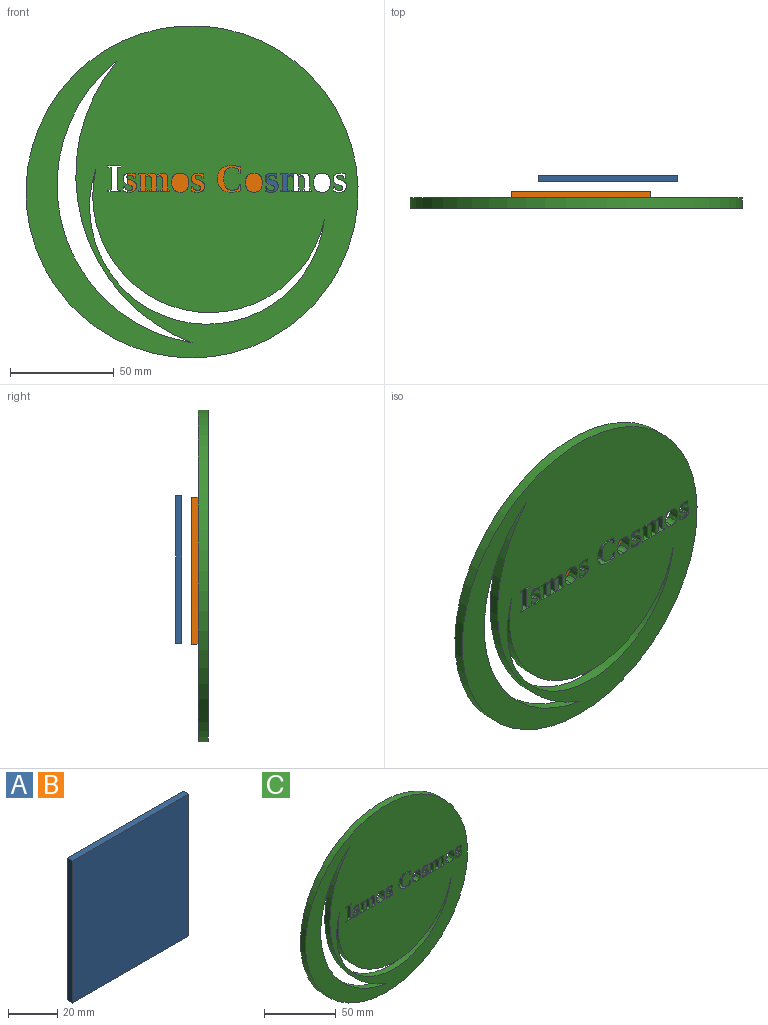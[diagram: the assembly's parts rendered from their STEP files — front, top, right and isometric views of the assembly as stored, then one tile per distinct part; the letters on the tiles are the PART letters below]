
ASSEMBLY  parts=3 mates=1
PART A: 6 faces, bbox 67x3x70.9 mm
  f0: plane 70.92x3mm, normal (1,0,0), area 212.8mm2, adj f1,f3,f4,f5
  f1: plane 66.96x3mm, normal (0,0,1), area 200.9mm2, adj f0,f2,f4,f5
  f2: plane 70.92x3mm, normal (-1,0,0), area 212.8mm2, adj f1,f3,f4,f5
  f3: plane 66.96x3mm, normal (0,0,-1), area 200.9mm2, adj f0,f2,f4,f5
  f4: plane 70.92x66.96mm, normal (0,-1,0), area 4749.3mm2, adj f0,f1,f2,f3
  f5: plane 70.92x66.96mm, normal (0,1,0), area 4749.3mm2, adj f0,f1,f2,f3
PART B: same geometry as A
PART C: 253 faces, bbox 160x5x160 mm
  f0: cylinder r=56.7mm len=113.03mm, axis (0,1,0), area 949.9mm2, adj f250,f251,f252
  f1: plane 10.62x5mm, normal (-1,0,0), area 53.1mm2, adj f2,f237,f251,f252
  f2: plane 5x1.6mm, normal (-0.15,0,-0.99), area 8.1mm2, adj f1,f3,f251,f252
  f3: plane 5x0.69mm, normal (-1,0,0), area 3.4mm2, adj f2,f4,f251,f252
  f4: plane 6.13x5mm, normal (0,0,1), area 30.7mm2, adj f3,f5,f251,f252
  f5: plane 5x0.69mm, normal (1,0,0), area 3.4mm2, adj f4,f6,f251,f252
  f6: plane 5x1.6mm, normal (0.15,0,-0.99), area 8.1mm2, adj f5,f7,f251,f252
  f7: plane 10.62x5mm, normal (1,0,0), area 53.1mm2, adj f6,f8,f251,f252
  f8: plane 5x1.6mm, normal (0.16,0,0.99), area 8.1mm2, adj f7,f9,f251,f252
  f9: plane 5x0.68mm, normal (1,0,0), area 3.4mm2, adj f8,f10,f251,f252
  f10: plane 6.13x5mm, normal (0,0,-1), area 30.7mm2, adj f9,f11,f251,f252
  f11: plane 5x0.68mm, normal (-1,0,0), area 3.4mm2, adj f10,f237,f251,f252
  f12: extruded ~5x1.71mm, area 9.2mm2, adj f13,f238,f251,f252
  f13: extruded ~5x2.21mm, area 12.3mm2, adj f12,f14,f251,f252
  f14: extruded ~5x2.61mm, area 13.9mm2, adj f13,f15,f251,f252
  f15: extruded ~5x1.56mm, area 7.8mm2, adj f14,f16,f251,f252
  f16: extruded ~5x1.29mm, area 6.7mm2, adj f15,f17,f251,f252
  f17: plane 5x2.38mm, normal (1,0,0), area 11.9mm2, adj f16,f18,f251,f252
  f18: plane 5x0.61mm, normal (0,0,-1), area 3.1mm2, adj f17,f19,f251,f252
  f19: plane 5x1.23mm, normal (-0.96,0,-0.28), area 6.4mm2, adj f18,f20,f251,f252
  f20: extruded ~5x0.86mm, area 5.1mm2, adj f19,f21,f251,f252
  f21: extruded ~5x1.08mm, area 5.5mm2, adj f20,f22,f251,f252
  f22: extruded ~5x1.21mm, area 6.4mm2, adj f21,f23,f251,f252
  f23: extruded ~5x0.89mm, area 5mm2, adj f22,f24,f251,f252
  f24: extruded ~5x0.82mm, area 4.7mm2, adj f23,f25,f251,f252
  f25: extruded ~5x1.67mm, area 9.1mm2, adj f24,f26,f251,f252
  f26: extruded ~5x1.91mm, area 11.3mm2, adj f25,f27,f251,f252
  f27: extruded ~5x1.79mm, area 9.6mm2, adj f26,f28,f251,f252
  f28: extruded ~5x1.9mm, area 10.9mm2, adj f27,f29,f251,f252
  f29: extruded ~5x2.28mm, area 12.2mm2, adj f28,f30,f251,f252
  f30: extruded ~5x2.58mm, area 13mm2, adj f29,f31,f251,f252
  f31: plane 5x2.24mm, normal (-1,0,0), area 11.2mm2, adj f30,f32,f251,f252
  f32: plane 5x0.61mm, normal (0,0,1), area 3.1mm2, adj f31,f33,f251,f252
  f33: plane 5x1.03mm, normal (0.96,0,0.28), area 5.3mm2, adj f32,f34,f251,f252
  f34: extruded ~5x0.76mm, area 4.4mm2, adj f33,f35,f251,f252
  f35: extruded ~5x0.93mm, area 4.7mm2, adj f34,f36,f251,f252
  f36: extruded ~5x0.99mm, area 5.3mm2, adj f35,f37,f251,f252
  f37: extruded ~5x0.75mm, area 4.2mm2, adj f36,f38,f251,f252
  f38: extruded ~5x0.81mm, area 4.7mm2, adj f37,f39,f251,f252
  f39: extruded ~5x1.65mm, area 9mm2, adj f38,f238,f251,f252
  f40: plane 5x0.77mm, normal (-0.99,0,-0.17), area 3.9mm2, adj f41,f239,f251,f252
  f41: plane 5x0.63mm, normal (0.46,0,-0.89), area 3.6mm2, adj f40,f42,f251,f252
  f42: extruded ~5x2.34mm, area 12.3mm2, adj f41,f43,f251,f252
  f43: extruded ~5x2.09mm, area 12.6mm2, adj f42,f44,f251,f252
  f44: extruded ~5x3.22mm, area 17.3mm2, adj f43,f45,f251,f252
  f45: extruded ~5x2.58mm, area 20.1mm2, adj f44,f46,f251,f252
  f46: plane 5.57x5mm, normal (-1,0,0), area 27.8mm2, adj f45,f47,f251,f252
  f47: plane 5x0.88mm, normal (-0.25,0,-0.97), area 4.5mm2, adj f46,f48,f251,f252
  f48: plane 5x0.61mm, normal (-1,0,0), area 3.1mm2, adj f47,f49,f251,f252
  f49: plane 5x4.35mm, normal (0,0,1), area 21.7mm2, adj f48,f50,f251,f252
  f50: plane 5x0.61mm, normal (1,0,0), area 3.1mm2, adj f49,f51,f251,f252
  f51: plane 5x0.78mm, normal (0.28,0,-0.96), area 4.1mm2, adj f50,f52,f251,f252
  f52: plane 5.2x5mm, normal (1,0,0), area 26mm2, adj f51,f53,f251,f252
  f53: extruded ~5x1.22mm, area 6.4mm2, adj f52,f54,f251,f252
  f54: extruded ~5x0.92mm, area 5.3mm2, adj f53,f55,f251,f252
  f55: extruded ~5x1.49mm, area 7.8mm2, adj f54,f56,f251,f252
  f56: extruded ~5x0.9mm, area 4.5mm2, adj f55,f57,f251,f252
  f57: plane 5.57x5mm, normal (-1,0,0), area 27.8mm2, adj f56,f58,f251,f252
  f58: plane 5x0.88mm, normal (-0.25,0,-0.97), area 4.5mm2, adj f57,f59,f251,f252
  f59: plane 5x0.61mm, normal (-1,0,0), area 3.1mm2, adj f58,f60,f251,f252
  f60: plane 5x4.35mm, normal (0,0,1), area 21.7mm2, adj f59,f61,f251,f252
  f61: plane 5x0.61mm, normal (1,0,0), area 3.1mm2, adj f60,f62,f251,f252
  f62: plane 5x0.78mm, normal (0.27,0,-0.96), area 4.1mm2, adj f61,f63,f251,f252
  f63: plane 5.2x5mm, normal (1,0,0), area 26mm2, adj f62,f64,f251,f252
  f64: extruded ~5x1.22mm, area 6.4mm2, adj f63,f65,f251,f252
  f65: extruded ~5x0.92mm, area 5.3mm2, adj f64,f66,f251,f252
  f66: extruded ~5x1.4mm, area 7.3mm2, adj f65,f67,f251,f252
  f67: plane 6.5x5mm, normal (-1,0,0), area 32.5mm2, adj f66,f68,f251,f252
  f68: plane 5x0.8mm, normal (-0.27,0,-0.96), area 4.1mm2, adj f67,f69,f251,f252
  f69: plane 5x0.61mm, normal (-1,0,0), area 3.1mm2, adj f68,f70,f251,f252
  f70: plane 5x4.35mm, normal (0,0,1), area 21.7mm2, adj f69,f71,f251,f252
  f71: plane 5x0.61mm, normal (1,0,0), area 3.1mm2, adj f70,f72,f251,f252
  f72: plane 5x0.86mm, normal (0.25,0,-0.97), area 4.4mm2, adj f71,f73,f251,f252
  f73: plane 7.08x5mm, normal (1,0,0), area 35.4mm2, adj f72,f74,f251,f252
  f74: plane 5x0.86mm, normal (0.25,0,0.97), area 4.4mm2, adj f73,f75,f251,f252
  f75: plane 5x0.62mm, normal (1,0,0), area 3.1mm2, adj f74,f239,f251,f252
  f76: extruded ~5x3.41mm, area 18.1mm2, adj f77,f240,f251,f252
  f77: extruded ~5x3.48mm, area 18.5mm2, adj f76,f78,f251,f252
  f78: extruded ~5x3.09mm, area 16.9mm2, adj f77,f79,f251,f252
  f79: extruded ~5x3mm, area 16.6mm2, adj f78,f80,f251,f252
  f80: extruded ~5x3.47mm, area 18.4mm2, adj f79,f81,f251,f252
  f81: extruded ~5x3.44mm, area 18.3mm2, adj f80,f82,f251,f252
  f82: extruded ~5x3.06mm, area 16.8mm2, adj f81,f240,f251,f252
  f83: extruded ~5x1.71mm, area 9.2mm2, adj f84,f241,f251,f252
  f84: extruded ~5x2.21mm, area 12.3mm2, adj f83,f85,f251,f252
  f85: extruded ~5x2.61mm, area 13.9mm2, adj f84,f86,f251,f252
  f86: extruded ~5x1.56mm, area 7.8mm2, adj f85,f87,f251,f252
  f87: extruded ~5x1.29mm, area 6.7mm2, adj f86,f88,f251,f252
  f88: plane 5x2.38mm, normal (1,0,0), area 11.9mm2, adj f87,f89,f251,f252
  f89: plane 5x0.61mm, normal (0,0,-1), area 3.1mm2, adj f88,f90,f251,f252
  f90: plane 5x1.23mm, normal (-0.96,0,-0.28), area 6.4mm2, adj f89,f91,f251,f252
  f91: extruded ~5x0.86mm, area 5.1mm2, adj f90,f92,f251,f252
  f92: extruded ~5x1.08mm, area 5.5mm2, adj f91,f93,f251,f252
  f93: extruded ~5x1.21mm, area 6.4mm2, adj f92,f94,f251,f252
  f94: extruded ~5x0.89mm, area 5mm2, adj f93,f95,f251,f252
  f95: extruded ~5x0.82mm, area 4.7mm2, adj f94,f96,f251,f252
  f96: extruded ~5x1.67mm, area 9.1mm2, adj f95,f97,f251,f252
  f97: extruded ~5x1.91mm, area 11.3mm2, adj f96,f98,f251,f252
  f98: extruded ~5x1.79mm, area 9.6mm2, adj f97,f99,f251,f252
  f99: extruded ~5x1.9mm, area 10.9mm2, adj f98,f100,f251,f252
  f100: extruded ~5x2.28mm, area 12.2mm2, adj f99,f101,f251,f252
  f101: extruded ~5x2.58mm, area 13mm2, adj f100,f102,f251,f252
  f102: plane 5x2.24mm, normal (-1,0,0), area 11.2mm2, adj f101,f103,f251,f252
  f103: plane 5x0.61mm, normal (0,0,1), area 3.1mm2, adj f102,f104,f251,f252
  f104: plane 5x1.03mm, normal (0.96,0,0.28), area 5.3mm2, adj f103,f105,f251,f252
  f105: extruded ~5x0.76mm, area 4.4mm2, adj f104,f106,f251,f252
  f106: extruded ~5x0.93mm, area 4.7mm2, adj f105,f107,f251,f252
  f107: extruded ~5x0.99mm, area 5.3mm2, adj f106,f108,f251,f252
  f108: extruded ~5x0.75mm, area 4.2mm2, adj f107,f109,f251,f252
  f109: extruded ~5x0.81mm, area 4.7mm2, adj f108,f110,f251,f252
  f110: extruded ~5x1.65mm, area 9mm2, adj f109,f241,f251,f252
  f111: plane 5x0.77mm, normal (-0.99,0,-0.17), area 3.9mm2, adj f112,f242,f251,f252
  f112: plane 5x0.63mm, normal (0.46,0,-0.89), area 3.6mm2, adj f111,f113,f251,f252
  f113: extruded ~5x2.34mm, area 12.3mm2, adj f112,f114,f251,f252
  f114: extruded ~5x2.09mm, area 12.6mm2, adj f113,f115,f251,f252
  f115: extruded ~5x3.22mm, area 17.3mm2, adj f114,f116,f251,f252
  f116: extruded ~5x2.58mm, area 20.1mm2, adj f115,f117,f251,f252
  f117: plane 5.57x5mm, normal (-1,0,0), area 27.8mm2, adj f116,f118,f251,f252
  f118: plane 5x0.88mm, normal (-0.25,0,-0.97), area 4.5mm2, adj f117,f119,f251,f252
  f119: plane 5x0.61mm, normal (-1,0,0), area 3.1mm2, adj f118,f120,f251,f252
  f120: plane 5x4.35mm, normal (0,0,1), area 21.7mm2, adj f119,f121,f251,f252
  f121: plane 5x0.61mm, normal (1,0,0), area 3.1mm2, adj f120,f122,f251,f252
  f122: plane 5x0.78mm, normal (0.28,0,-0.96), area 4.1mm2, adj f121,f123,f251,f252
  f123: plane 5.2x5mm, normal (1,0,0), area 26mm2, adj f122,f124,f251,f252
  f124: extruded ~5x1.22mm, area 6.4mm2, adj f123,f125,f251,f252
  f125: extruded ~5x0.92mm, area 5.3mm2, adj f124,f126,f251,f252
  f126: extruded ~5x1.49mm, area 7.8mm2, adj f125,f127,f251,f252
  f127: extruded ~5x0.9mm, area 4.5mm2, adj f126,f128,f251,f252
  f128: plane 5.57x5mm, normal (-1,0,0), area 27.8mm2, adj f127,f129,f251,f252
  f129: plane 5x0.88mm, normal (-0.25,0,-0.97), area 4.5mm2, adj f128,f130,f251,f252
  f130: plane 5x0.61mm, normal (-1,0,0), area 3.1mm2, adj f129,f131,f251,f252
  f131: plane 5x4.35mm, normal (0,0,1), area 21.7mm2, adj f130,f132,f251,f252
  f132: plane 5x0.61mm, normal (1,0,0), area 3.1mm2, adj f131,f133,f251,f252
  f133: plane 5x0.78mm, normal (0.27,0,-0.96), area 4.1mm2, adj f132,f134,f251,f252
  f134: plane 5.2x5mm, normal (1,0,0), area 26mm2, adj f133,f135,f251,f252
  f135: extruded ~5x1.22mm, area 6.4mm2, adj f134,f136,f251,f252
  f136: extruded ~5x0.92mm, area 5.3mm2, adj f135,f137,f251,f252
  f137: extruded ~5x1.4mm, area 7.3mm2, adj f136,f138,f251,f252
  f138: plane 6.5x5mm, normal (-1,0,0), area 32.5mm2, adj f137,f139,f251,f252
  f139: plane 5x0.8mm, normal (-0.27,0,-0.96), area 4.1mm2, adj f138,f140,f251,f252
  f140: plane 5x0.61mm, normal (-1,0,0), area 3.1mm2, adj f139,f141,f251,f252
  f141: plane 5x4.35mm, normal (0,0,1), area 21.7mm2, adj f140,f142,f251,f252
  f142: plane 5x0.61mm, normal (1,0,0), area 3.1mm2, adj f141,f143,f251,f252
  f143: plane 5x0.86mm, normal (0.25,0,-0.97), area 4.4mm2, adj f142,f144,f251,f252
  f144: plane 7.08x5mm, normal (1,0,0), area 35.4mm2, adj f143,f145,f251,f252
  f145: plane 5x0.86mm, normal (0.25,0,0.97), area 4.4mm2, adj f144,f146,f251,f252
  f146: plane 5x0.62mm, normal (1,0,0), area 3.1mm2, adj f145,f242,f251,f252
  f147: extruded ~5x3.41mm, area 18.1mm2, adj f148,f243,f251,f252
  f148: extruded ~5x3.48mm, area 18.5mm2, adj f147,f149,f251,f252
  f149: extruded ~5x3.09mm, area 16.9mm2, adj f148,f150,f251,f252
  f150: extruded ~5x3mm, area 16.6mm2, adj f149,f151,f251,f252
  f151: extruded ~5x3.47mm, area 18.4mm2, adj f150,f152,f251,f252
  f152: extruded ~5x3.44mm, area 18.3mm2, adj f151,f153,f251,f252
  f153: extruded ~5x3.06mm, area 16.8mm2, adj f152,f243,f251,f252
  f154: extruded ~5x1.71mm, area 9.2mm2, adj f155,f245,f251,f252
  f155: extruded ~5x2.21mm, area 12.3mm2, adj f154,f156,f251,f252
  f156: extruded ~5x2.61mm, area 13.9mm2, adj f155,f157,f251,f252
  f157: extruded ~5x1.56mm, area 7.8mm2, adj f156,f158,f251,f252
  f158: extruded ~5x1.29mm, area 6.7mm2, adj f157,f159,f251,f252
  f159: plane 5x2.38mm, normal (1,0,0), area 11.9mm2, adj f158,f160,f251,f252
  f160: plane 5x0.61mm, normal (0,0,-1), area 3.1mm2, adj f159,f161,f251,f252
  f161: plane 5x1.23mm, normal (-0.96,0,-0.28), area 6.4mm2, adj f160,f162,f251,f252
  f162: extruded ~5x0.86mm, area 5.1mm2, adj f161,f163,f251,f252
  f163: extruded ~5x1.08mm, area 5.5mm2, adj f162,f164,f251,f252
  f164: extruded ~5x1.21mm, area 6.4mm2, adj f163,f165,f251,f252
  f165: extruded ~5x0.89mm, area 5mm2, adj f164,f166,f251,f252
  f166: extruded ~5x0.82mm, area 4.7mm2, adj f165,f167,f251,f252
  f167: extruded ~5x1.67mm, area 9.1mm2, adj f166,f168,f251,f252
  f168: extruded ~5x1.91mm, area 11.3mm2, adj f167,f169,f251,f252
  f169: extruded ~5x1.79mm, area 9.6mm2, adj f168,f170,f251,f252
  f170: extruded ~5x1.9mm, area 10.9mm2, adj f169,f171,f251,f252
  f171: extruded ~5x2.28mm, area 12.2mm2, adj f170,f172,f251,f252
  f172: extruded ~5x2.58mm, area 13mm2, adj f171,f173,f251,f252
  f173: plane 5x2.24mm, normal (-1,0,0), area 11.2mm2, adj f172,f174,f251,f252
  f174: plane 5x0.61mm, normal (0,0,1), area 3.1mm2, adj f173,f175,f251,f252
  f175: plane 5x1.03mm, normal (0.96,0,0.28), area 5.3mm2, adj f174,f176,f251,f252
  f176: extruded ~5x0.76mm, area 4.4mm2, adj f175,f177,f251,f252
  f177: extruded ~5x0.93mm, area 4.7mm2, adj f176,f178,f251,f252
  f178: extruded ~5x0.99mm, area 5.3mm2, adj f177,f179,f251,f252
  f179: extruded ~5x0.75mm, area 4.2mm2, adj f178,f180,f251,f252
  f180: extruded ~5x0.81mm, area 4.7mm2, adj f179,f181,f251,f252
  f181: extruded ~5x1.65mm, area 9mm2, adj f180,f245,f251,f252
  f182: extruded ~5x3.41mm, area 18.1mm2, adj f183,f246,f251,f252
  f183: extruded ~5x3.48mm, area 18.5mm2, adj f182,f184,f251,f252
  f184: extruded ~5x3.09mm, area 16.9mm2, adj f183,f185,f251,f252
  f185: extruded ~5x3mm, area 16.6mm2, adj f184,f186,f251,f252
  f186: extruded ~5x3.47mm, area 18.4mm2, adj f185,f187,f251,f252
  f187: extruded ~5x3.44mm, area 18.3mm2, adj f186,f188,f251,f252
  f188: extruded ~5x3.06mm, area 16.8mm2, adj f187,f246,f251,f252
  f189: extruded ~5x2.49mm, area 12.5mm2, adj f190,f247,f251,f252
  f190: extruded ~5x4.9mm, area 26.5mm2, adj f189,f191,f251,f252
  f191: extruded ~5x4.62mm, area 25.4mm2, adj f190,f192,f251,f252
  f192: extruded ~5x4.87mm, area 26.4mm2, adj f191,f193,f251,f252
  f193: extruded ~5x4.97mm, area 26.9mm2, adj f192,f194,f251,f252
  f194: extruded ~5x4.5mm, area 22.8mm2, adj f193,f195,f251,f252
  f195: plane 5x3mm, normal (-1,0,-0.02), area 15mm2, adj f194,f196,f251,f252
  f196: plane 5x0.84mm, normal (0,0,1), area 4.2mm2, adj f195,f197,f251,f252
  f197: plane 5x1.81mm, normal (0.99,0,0.14), area 9.1mm2, adj f196,f198,f251,f252
  f198: extruded ~5x2.86mm, area 15.1mm2, adj f197,f199,f251,f252
  f199: extruded ~5x3.16mm, area 17.8mm2, adj f198,f200,f251,f252
  f200: extruded ~5x4.18mm, area 21.8mm2, adj f199,f201,f251,f252
  f201: extruded ~5x3.98mm, area 21mm2, adj f200,f202,f251,f252
  f202: extruded ~5x3.04mm, area 17.3mm2, adj f201,f203,f251,f252
  f203: extruded ~5x1.84mm, area 9.3mm2, adj f202,f204,f251,f252
  f204: extruded ~5x1.23mm, area 7mm2, adj f203,f205,f251,f252
  f205: plane 5x2.05mm, normal (0.99,0,-0.14), area 10.4mm2, adj f204,f206,f251,f252
  f206: plane 5x0.85mm, normal (0,0,-1), area 4.2mm2, adj f205,f207,f251,f252
  f207: plane 5x3.17mm, normal (-1,0,0.02), area 15.8mm2, adj f206,f247,f251,f252
  f208: extruded ~5x1.71mm, area 9.2mm2, adj f209,f248,f251,f252
  f209: extruded ~5x2.21mm, area 12.3mm2, adj f208,f210,f251,f252
  f210: extruded ~5x2.61mm, area 13.9mm2, adj f209,f211,f251,f252
  f211: extruded ~5x1.56mm, area 7.8mm2, adj f210,f212,f251,f252
  f212: extruded ~5x1.29mm, area 6.7mm2, adj f211,f213,f251,f252
  f213: plane 5x2.38mm, normal (1,0,0), area 11.9mm2, adj f212,f214,f251,f252
  f214: plane 5x0.61mm, normal (0,0,-1), area 3.1mm2, adj f213,f215,f251,f252
  f215: plane 5x1.23mm, normal (-0.96,0,-0.28), area 6.4mm2, adj f214,f216,f251,f252
  f216: extruded ~5x0.86mm, area 5.1mm2, adj f215,f217,f251,f252
  f217: extruded ~5x1.08mm, area 5.5mm2, adj f216,f218,f251,f252
  f218: extruded ~5x1.21mm, area 6.4mm2, adj f217,f219,f251,f252
  f219: extruded ~5x0.89mm, area 5mm2, adj f218,f220,f251,f252
  f220: extruded ~5x0.82mm, area 4.7mm2, adj f219,f221,f251,f252
  f221: extruded ~5x1.67mm, area 9.1mm2, adj f220,f222,f251,f252
  f222: extruded ~5x1.91mm, area 11.3mm2, adj f221,f223,f251,f252
  f223: extruded ~5x1.79mm, area 9.6mm2, adj f222,f224,f251,f252
  f224: extruded ~5x1.9mm, area 10.9mm2, adj f223,f225,f251,f252
  f225: extruded ~5x2.28mm, area 12.2mm2, adj f224,f226,f251,f252
  f226: extruded ~5x2.58mm, area 13mm2, adj f225,f227,f251,f252
  f227: plane 5x2.24mm, normal (-1,0,0), area 11.2mm2, adj f226,f228,f251,f252
  f228: plane 5x0.61mm, normal (0,0,1), area 3.1mm2, adj f227,f229,f251,f252
  f229: plane 5x1.03mm, normal (0.96,0,0.28), area 5.3mm2, adj f228,f230,f251,f252
  f230: extruded ~5x0.76mm, area 4.4mm2, adj f229,f231,f251,f252
  f231: extruded ~5x0.93mm, area 4.7mm2, adj f230,f232,f251,f252
  f232: extruded ~5x0.99mm, area 5.3mm2, adj f231,f233,f251,f252
  f233: extruded ~5x0.75mm, area 4.2mm2, adj f232,f234,f251,f252
  f234: extruded ~5x0.81mm, area 4.7mm2, adj f233,f235,f251,f252
  f235: extruded ~5x1.65mm, area 9mm2, adj f234,f248,f251,f252
  f236: cylinder r=76.7mm len=135.67mm, axis (0,1,0), area 887.2mm2, adj f249,f251,f252
  f237: plane 5x1.6mm, normal (-0.16,0,0.99), area 8.1mm2, adj f1,f11,f251,f252
  f238: extruded ~5x1.93mm, area 11.2mm2, adj f12,f39,f251,f252
  f239: plane 5x3.4mm, normal (0,0,-1), area 17mm2, adj f40,f75,f251,f252
  f240: extruded ~5x3.05mm, area 16.9mm2, adj f76,f82,f251,f252
  f241: extruded ~5x1.93mm, area 11.2mm2, adj f83,f110,f251,f252
  f242: plane 5x3.4mm, normal (0,0,-1), area 17mm2, adj f111,f146,f251,f252
  f243: extruded ~5x3.05mm, area 16.9mm2, adj f147,f153,f251,f252
  f244: cylinder r=80mm len=160mm, axis (0,1,0), area 2513.3mm2, adj f251,f252
  f245: extruded ~5x1.93mm, area 11.2mm2, adj f154,f181,f251,f252
  f246: extruded ~5x3.05mm, area 16.9mm2, adj f182,f188,f251,f252
  f247: extruded ~5x2.18mm, area 11.3mm2, adj f189,f207,f251,f252
  f248: extruded ~5x1.93mm, area 11.2mm2, adj f208,f235,f251,f252
  f249: cylinder r=86.31mm len=135.67mm, axis (0,1,0), area 820.2mm2, adj f236,f251,f252
  f250: cylinder r=56.39mm len=111.54mm, axis (0,1,0), area 890.4mm2, adj f0,f251,f252
  f251: plane 160x160mm, normal (0,-1,0), area 17780.9mm2, adj f0,f1,f2,f3,f4,f5,f6,f7
  f252: plane 160x160mm, normal (0,1,0), area 17780.9mm2, adj f0,f1,f2,f3,f4,f5,f6,f7
PLACE A t=(-2.52,43.55,0.66)mm
PLACE B t=(-15.34,35.74,0.05)mm
PLACE C t=(-17.37,32.74,-3.97)mm
MATE fastened C.f252 <-> B.f4  axis (0,1,0) through (-14.85,32.74,-1.54)mm
